# Revit family: E_Actuator_F_MEPcontent_Oventrop_Aktor T 2P
name_source: partatom
category: Electrical Fixtures
revit_build: Autodesk Revit MEP 2015 (Build: 20140606_1530(x64)
units: mm (PartAtom-declared; Revit-internal decimal feet)

## types (2) — shared parameters
Ambient Temperature = 0 °C up to 60 °C
Black = Color RGB 060-060-060
Cap Length = 6.2 mm  [stored 0.0203412 ft]
Cap Length 2 = 8.5 mm  [stored 0.0278871 ft]
Closing/Opening Time = about 5 min.
Content Supplier URL = www.mepcontent.eu
Custom = No
Default Elevation = 1219.2 mm  [stored 4 ft]
EMCS Version = 2.0
ETIM Article Class = EC010193
Family Version = 10.14
Fluid Temperature = 0 °C up to 100 °C
Grey = Color RGB 100-100-100
Height = 50.3 mm  [stored 0.165026 ft]
Height 2 = 52.2 mm  [stored 0.17126 ft]
IFCExportAs = IfcActuatorType
IFCExportType = ELECTRICACTUATOR
Length = 48.4 mm
MEPcontent Class = ACTUATOR
Manufacturer = Oventrop
Manufacturer URL = http://www.oventrop.com
Operating Power = > 90 N
Piston Stroke = 5 mm
Product Line = Oventrop
Protection = IP 54 in any position
Revit Version = 2015
Standard Connection = Yes
Storage Temperature = -25 °C up to +60 °C
URL = www.stabiplan.com
White = Color RGB 245-245-245
Width = 44.3 mm  [stored 0.145341 ft]

## per-type parameters (varying)
| type | Article Description | Auxiliary Switch, Switching Current | Auxiliary Switch, Switching Point | Connecting Cable | Continuous Current | Description | GTIN | Manufacturer Art. No. | Protective System | Start Up Load | Voltage |
| 2415 | Electrothermal actuator "Aktor T 2P" "H NC", 230 V, closed with current "off", two point, M 30 x 1.5 | 5 A resistive load,  1 A inductive load with 230 V AC | about 2 mm | 2 x 0.75 mm² , 1 m long  4 x 0.75 mm² | 4.5 mA | Electrothermal actuator "Aktor T 2P" "H NC", 230 V, closed with current "off", two point, M 30 x 1.5 | 4026755415520 | 1012415 | II according to EN 60730 | < 550 mA for a max. of 100 ms | 230 V |
| 2416 | Electrothermal actuator "Aktor T 2P" "L NC", 24 V, closed with current "off", two point, M 30 x 1.5 |  |  | 2 x 0.75 mm², 1 m long | 45 mA | Electrothermal actuator "Aktor T 2P" "L NC", 24 V, closed with current "off", two point, M 30 x 1.5 | 4026755415537 | 1012416 | III according to EN 60730 | < 300 mA for a max. of 2 min. | 24 V |

note: column(s) folded — value = type name in every type: Article Type, Model

note: [stored X ft] marks values corroborated as IEEE doubles in the binary element streams (Revit-internal decimal feet)

## geometry (parser evidence)
native form markers: Sweep x2
no freeform markers — native parametric forms only
